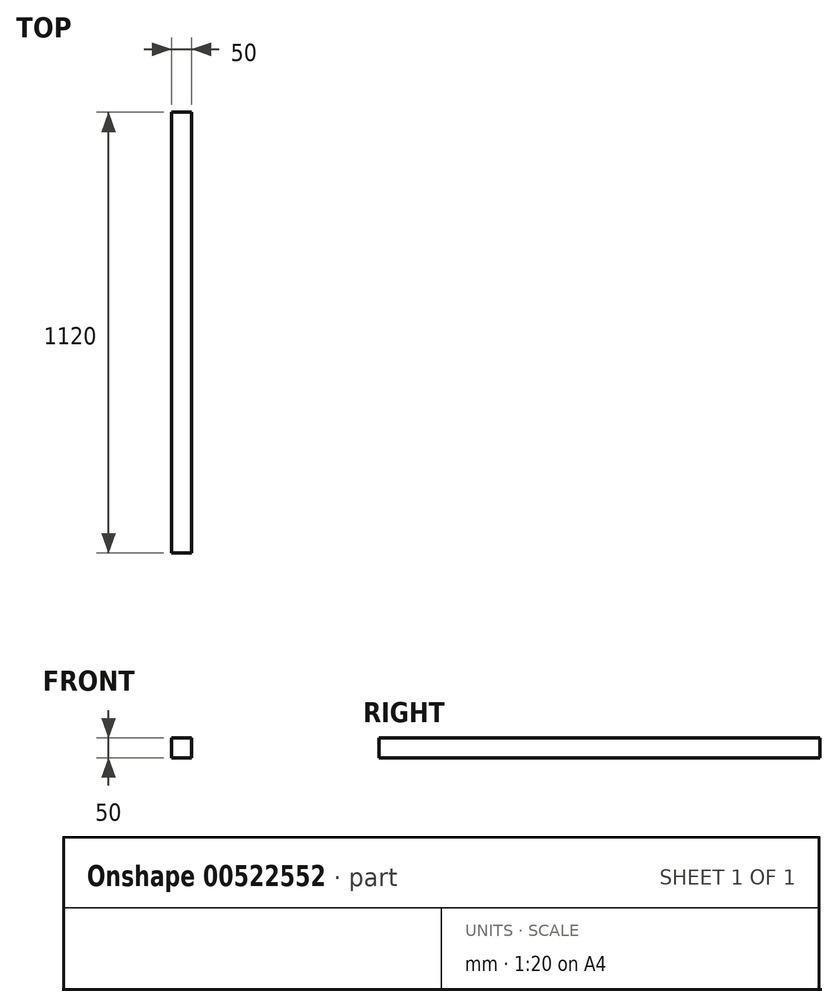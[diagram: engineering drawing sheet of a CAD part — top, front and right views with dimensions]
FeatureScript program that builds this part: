
annotation { "Feature Type Name" : "Feature", "Feature Type Description" : "" }
export const myFeature = defineFeature(function(context is Context, id is Id, definition is map)
    precondition{}
    {
        {
            var Q0;
            Q0=qCreatedBy(makeId("Front.planeOp"),FACE);
            var sketch = newSketch(context, id + "F0", { "sketchPlane" : qUnion([Q0])});
            skLineSegment(sketch, "E0.bottom", {"start": v(0, 0) * mm, "end": v(-50, 0) * mm});
            skLineSegment(sketch, "E0.top", {"start": v(0, 50) * mm, "end": v(-50, 50) * mm});
            skLineSegment(sketch, "E0.left", {"start": v(0, 0) * mm, "end": v(0, 50) * mm});
            skLineSegment(sketch, "E0.right", {"start": v(-50, 0) * mm, "end": v(-50, 50) * mm});
            skSolve(sketch);
        }
        {
            var Q0;
            Q0=qSketchRegion(id+"F0",true);
            extrude(context, id + "F1", {"entities" : qUnion([Q0]), "depth" : 1120 * mm, "offsetDistance" : 25 * mm});
        }
    });
